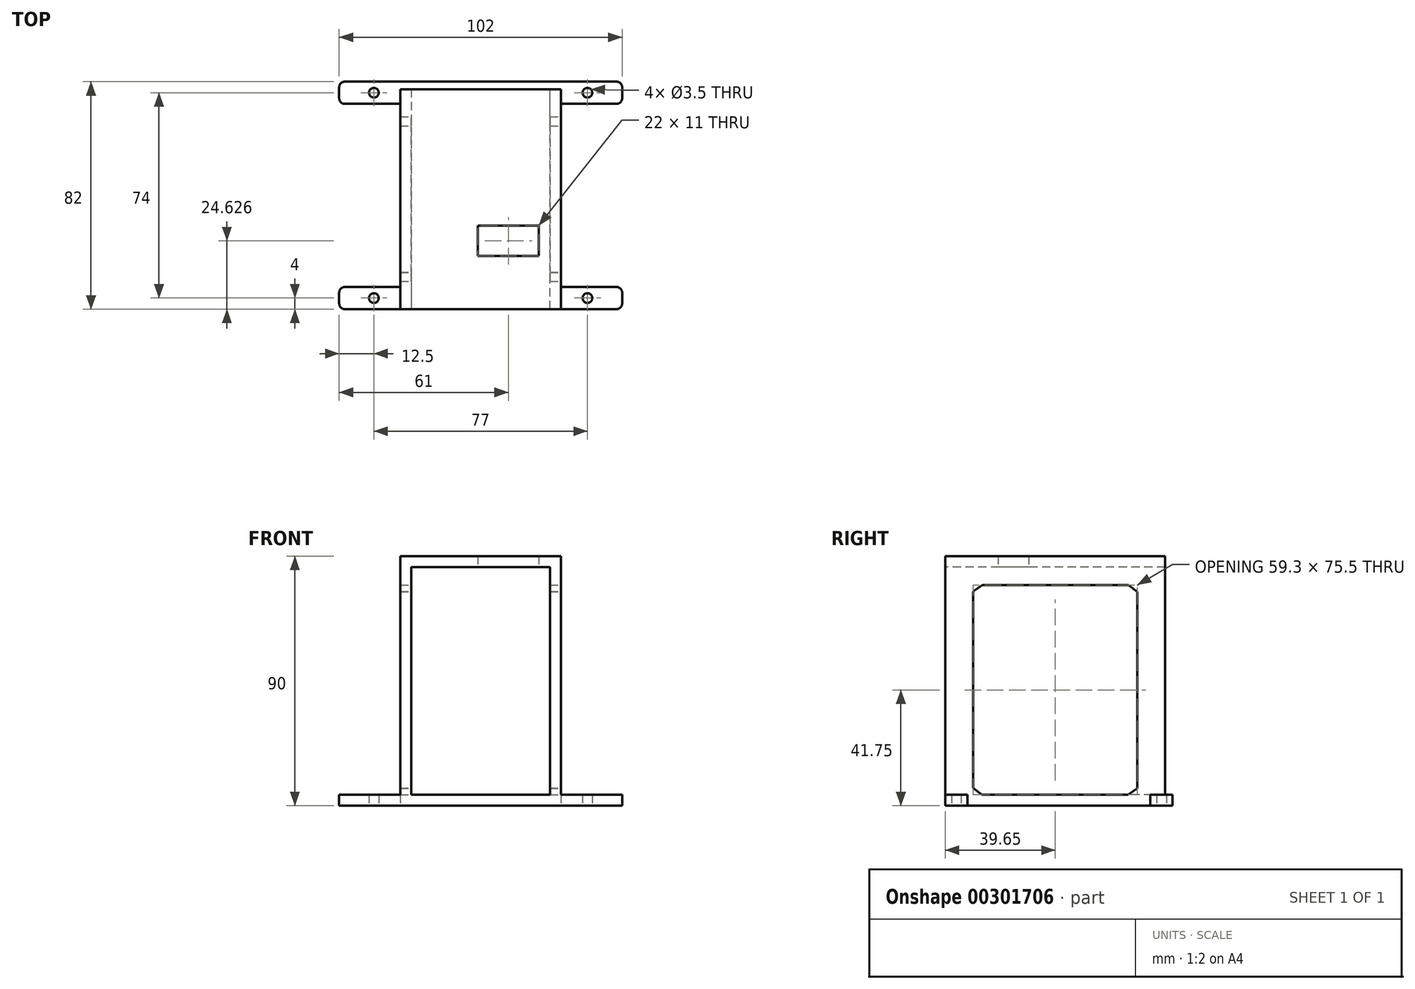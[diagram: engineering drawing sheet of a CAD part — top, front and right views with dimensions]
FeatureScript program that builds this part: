
annotation { "Feature Type Name" : "Feature", "Feature Type Description" : "" }
export const myFeature = defineFeature(function(context is Context, id is Id, definition is map)
    precondition{}
    {
        {
            var Q0;
            Q0=qCreatedBy(makeId("Top.planeOp"),FACE);
            var sketch = newSketch(context, id + "F0", { "sketchPlane" : qUnion([Q0])});
            skPoint(sketch, "E0.middle", {"position": v(45, 2.5) * mm});
            skPoint(sketch, "E1.orphan", {"position": v(-8, 87) * mm});
            skPoint(sketch, "E2.orphan", {"position": v(98, 87) * mm});
            skPoint(sketch, "E3.orphan", {"position": v(-8, 10) * mm});
            skPoint(sketch, "E4.orphan", {"position": v(0, 0) * mm});
            skPoint(sketch, "E5.orphan", {"position": v(90, 0) * mm});
            skPoint(sketch, "E6", {"position": v(45, 104.4) * mm});
            skPoint(sketch, "E7.end.orphan", {"position": v(95.45, 87) * mm});
            skPoint(sketch, "E8.bottom.end.orphan", {"position": v(33.96, 3.68) * mm});
            skLineSegment(sketch, "E9.bottom", {"start": v(19, 89.45) * mm, "end": v(71, 89.45) * mm});
            skLineSegment(sketch, "E9.top", {"start": v(19, 7.45) * mm, "end": v(71, 7.45) * mm});
            skLineSegment(sketch, "E9.left", {"start": v(19, 81.45) * mm, "end": v(19, 15.45) * mm});
            skLineSegment(sketch, "E9.right", {"start": v(71, 81.45) * mm, "end": v(71, 15.45) * mm});
            skLineSegment(sketch, "E10.bottom", {"start": v(71, 89.45) * mm, "end": v(96, 89.45) * mm});
            skLineSegment(sketch, "E10.top", {"start": v(71, 81.45) * mm, "end": v(96, 81.45) * mm});
            skLineSegment(sketch, "E10.right", {"start": v(96, 89.45) * mm, "end": v(96, 81.45) * mm});
            skLineSegment(sketch, "E11.bottom", {"start": v(19, 89.45) * mm, "end": v(-6, 89.45) * mm});
            skLineSegment(sketch, "E11.top", {"start": v(19, 81.45) * mm, "end": v(-6, 81.45) * mm});
            skLineSegment(sketch, "E11.right", {"start": v(-6, 89.45) * mm, "end": v(-6, 81.45) * mm});
            skLineSegment(sketch, "E12.bottom", {"start": v(19, 7.45) * mm, "end": v(-6, 7.45) * mm});
            skLineSegment(sketch, "E12.top", {"start": v(19, 15.45) * mm, "end": v(-6, 15.45) * mm});
            skLineSegment(sketch, "E12.right", {"start": v(-6, 7.45) * mm, "end": v(-6, 15.45) * mm});
            skLineSegment(sketch, "E13.bottom", {"start": v(71, 7.45) * mm, "end": v(96, 7.45) * mm});
            skLineSegment(sketch, "E13.top", {"start": v(71, 15.45) * mm, "end": v(96, 15.45) * mm});
            skLineSegment(sketch, "E13.right", {"start": v(96, 7.45) * mm, "end": v(96, 15.45) * mm});
            skLineSegment(sketch, "E14", {"start": v(19, 7.45) * mm, "end": v(-6, 15.45) * mm, "construction": true});
            skLineSegment(sketch, "E15", {"start": v(-6, 7.45) * mm, "end": v(19, 15.45) * mm, "construction": true});
            skCircle(sketch, "E16", {"center": v(6.5, 11.45) * mm, "radius": 1.75 * mm});
            skLineSegment(sketch, "E17", {"start": v(96, 7.45) * mm, "end": v(71, 15.45) * mm, "construction": true});
            skLineSegment(sketch, "E18", {"start": v(71, 7.45) * mm, "end": v(96, 15.45) * mm, "construction": true});
            skCircle(sketch, "E19", {"center": v(83.5, 11.45) * mm, "radius": 1.75 * mm});
            skLineSegment(sketch, "E20", {"start": v(96, 81.45) * mm, "end": v(71, 89.45) * mm, "construction": true});
            skLineSegment(sketch, "E21", {"start": v(71, 81.45) * mm, "end": v(96, 89.45) * mm, "construction": true});
            skCircle(sketch, "E22", {"center": v(83.5, 85.45) * mm, "radius": 1.75 * mm});
            skLineSegment(sketch, "E23", {"start": v(19, 81.45) * mm, "end": v(-6, 89.45) * mm, "construction": true});
            skLineSegment(sketch, "E24", {"start": v(-6, 81.45) * mm, "end": v(19, 89.45) * mm, "construction": true});
            skCircle(sketch, "E25", {"center": v(6.5, 85.45) * mm, "radius": 1.75 * mm});
            skSolve(sketch);
        }
        {
            var Q0;
            Q0=makeQuery(id+"F0.imprint","IMPRINT",FACE,{"disambiguationData":[TD([[makeQuery(id+"F0.imprint","IMPRINT",EDGE,{"derivedFrom":sQuery(id+"F0.wireOp",EDGE,"E9.bottom")}),-1.0]])]});
            extrude(context, id + "F1", {"entities" : qUnion([Q0]), "depth" : 4 * mm, "offsetDistance" : 25 * mm});
        }
        {
            var Q0;
            Q0=makeQuery(id+"F1.opExtrude","CAP_FACE",FACE,{"disambiguationData":[OSD([sQuery(id+"F0.wireOp",EDGE,"E9.bottom"),sQuery(id+"F0.wireOp",EDGE,"E9.top"),sQuery(id+"F0.wireOp",EDGE,"E9.left"),sQuery(id+"F0.wireOp",EDGE,"E9.right"),sQuery(id+"F0.wireOp",EDGE,"E10.bottom"),sQuery(id+"F0.wireOp",EDGE,"E10.top"),sQuery(id+"F0.wireOp",EDGE,"E10.right"),sQuery(id+"F0.wireOp",EDGE,"E11.bottom"),sQuery(id+"F0.wireOp",EDGE,"E11.top"),sQuery(id+"F0.wireOp",EDGE,"E11.right"),sQuery(id+"F0.wireOp",EDGE,"E12.bottom"),sQuery(id+"F0.wireOp",EDGE,"E12.top"),sQuery(id+"F0.wireOp",EDGE,"E12.right"),sQuery(id+"F0.wireOp",EDGE,"E13.bottom"),sQuery(id+"F0.wireOp",EDGE,"E13.top"),sQuery(id+"F0.wireOp",EDGE,"E13.right"),sQuery(id+"F0.wireOp",EDGE,"E16"),sQuery(id+"F0.wireOp",EDGE,"E19"),sQuery(id+"F0.wireOp",EDGE,"E22"),sQuery(id+"F0.wireOp",EDGE,"E25")])],"isStart":false});
            cPlane(context, id + "F2", {"entities" : qUnion([Q0]), "cplaneType" : CPlaneType.OFFSET, "offset" : 0 * mm, "width" : 150 * mm, "height" : 150 * mm});
        }
        {
            var Q0;
            Q0=qCreatedBy(id+"F2.planeOp",FACE);
            var sketch = newSketch(context, id + "F3", { "sketchPlane" : qUnion([Q0])});
            skLineSegment(sketch, "E26.bottom", {"start": v(68, 7.45) * mm, "end": v(71, 7.45) * mm});
            skLineSegment(sketch, "E26.top", {"start": v(68, 86.75) * mm, "end": v(71, 86.75) * mm});
            skLineSegment(sketch, "E26.left", {"start": v(68, 7.45) * mm, "end": v(68, 86.75) * mm});
            skLineSegment(sketch, "E26.right", {"start": v(71, 7.45) * mm, "end": v(71, 86.75) * mm});
            skLineSegment(sketch, "E27.bottom", {"start": v(19, 86.75) * mm, "end": v(22, 86.75) * mm});
            skLineSegment(sketch, "E27.top", {"start": v(19, 7.45) * mm, "end": v(22, 7.45) * mm});
            skLineSegment(sketch, "E27.left", {"start": v(19, 86.75) * mm, "end": v(19, 7.45) * mm});
            skLineSegment(sketch, "E27.right", {"start": v(22, 86.75) * mm, "end": v(22, 7.45) * mm});
            skSolve(sketch);
        }
        {
            var Q0;
            Q0=makeQuery(id+"F3.imprint","IMPRINT",FACE,{"disambiguationData":[TD([[makeQuery(id+"F3.imprint","IMPRINT",EDGE,{"derivedFrom":sQuery(id+"F3.wireOp",EDGE,"E27.bottom")}),-1.0]])]});
            var Q1;
            Q1=makeQuery(id+"F3.imprint","IMPRINT",FACE,{"disambiguationData":[TD([[makeQuery(id+"F3.imprint","IMPRINT",EDGE,{"derivedFrom":sQuery(id+"F3.wireOp",EDGE,"E26.bottom")}),1.0]])]});
            extrude(context, id + "F4", {"entities" : qUnion([Q0, Q1]), "operationType" : NewBodyOperationType.ADD, "depth" : 82 * mm, "offsetDistance" : 25 * mm});
        }
        {
            var Q0;
            Q0=makeQuery(id+"F4.opExtrude","SWEPT_FACE",FACE,{"disambiguationData":[OSD([sQuery(id+"F3.wireOp",EDGE,"E27.right")])]});
            extrude(context, id + "F5", {"entities" : qUnion([Q0]), "operationType" : NewBodyOperationType.REMOVE, "oppositeDirection" : true, "depth" : 2 * mm, "offsetDistance" : 25 * mm});
        }
        {
            var Q0;
            Q0=makeQuery(id+"F4.opExtrude","SWEPT_FACE",FACE,{"disambiguationData":[OSD([sQuery(id+"F3.wireOp",EDGE,"E26.left")])]});
            extrude(context, id + "F6", {"entities" : qUnion([Q0]), "operationType" : NewBodyOperationType.REMOVE, "oppositeDirection" : true, "depth" : 2 * mm, "offsetDistance" : 25 * mm});
        }
        {
            var Q0;
            Q0=makeQuery(id+"F4.boolean.opBoolean","MERGE",FACE,{"derivedFrom":[makeQuery(id+"F1.opExtrude","SWEPT_FACE",FACE,{"disambiguationData":[OSD([sQuery(id+"F0.wireOp",EDGE,"E9.right")])]}),makeQuery(id+"F4.opExtrude","SWEPT_FACE",FACE,{"disambiguationData":[OSD([sQuery(id+"F3.wireOp",EDGE,"E26.right")])]})]});
            extrude(context, id + "F7", {"entities" : qUnion([Q0]), "operationType" : NewBodyOperationType.ADD, "depth" : 3 * mm, "offsetDistance" : 25 * mm});
        }
        {
            var Q0;
            Q0=makeQuery(id+"F4.boolean.opBoolean","MERGE",FACE,{"derivedFrom":[makeQuery(id+"F1.opExtrude","SWEPT_FACE",FACE,{"disambiguationData":[OSD([sQuery(id+"F0.wireOp",EDGE,"E9.left")])]}),makeQuery(id+"F4.opExtrude","SWEPT_FACE",FACE,{"disambiguationData":[OSD([sQuery(id+"F3.wireOp",EDGE,"E27.left")])]})]});
            extrude(context, id + "F8", {"entities" : qUnion([Q0]), "operationType" : NewBodyOperationType.ADD, "depth" : 3 * mm, "offsetDistance" : 25 * mm});
        }
        {
            var Q0;
            Q0=makeQuery(id+"F1.opExtrude","SWEPT_EDGE",EDGE,{"disambiguationData":[OSD([sQuery(id+"F0.wireOp",EDGE,"E10.top"),sQuery(id+"F0.wireOp",EDGE,"E10.right")])]});
            var Q1;
            Q1=makeQuery(id+"F1.opExtrude","SWEPT_EDGE",EDGE,{"disambiguationData":[OSD([sQuery(id+"F0.wireOp",EDGE,"E10.bottom"),sQuery(id+"F0.wireOp",EDGE,"E10.right")])]});
            var Q2;
            Q2=makeQuery(id+"F1.opExtrude","SWEPT_EDGE",EDGE,{"disambiguationData":[OSD([sQuery(id+"F0.wireOp",EDGE,"E13.top"),sQuery(id+"F0.wireOp",EDGE,"E13.right")])]});
            var Q3;
            Q3=makeQuery(id+"F1.opExtrude","SWEPT_EDGE",EDGE,{"disambiguationData":[OSD([sQuery(id+"F0.wireOp",EDGE,"E13.bottom"),sQuery(id+"F0.wireOp",EDGE,"E13.right")])]});
            var Q4;
            Q4=makeQuery(id+"F1.opExtrude","SWEPT_EDGE",EDGE,{"disambiguationData":[OSD([sQuery(id+"F0.wireOp",EDGE,"E12.bottom"),sQuery(id+"F0.wireOp",EDGE,"E12.right")])]});
            var Q5;
            Q5=makeQuery(id+"F1.opExtrude","SWEPT_EDGE",EDGE,{"disambiguationData":[OSD([sQuery(id+"F0.wireOp",EDGE,"E11.bottom"),sQuery(id+"F0.wireOp",EDGE,"E11.right")])]});
            var Q6;
            Q6=makeQuery(id+"F1.opExtrude","SWEPT_EDGE",EDGE,{"disambiguationData":[OSD([sQuery(id+"F0.wireOp",EDGE,"E11.top"),sQuery(id+"F0.wireOp",EDGE,"E11.right")])]});
            var Q7;
            Q7=makeQuery(id+"F1.opExtrude","SWEPT_EDGE",EDGE,{"disambiguationData":[OSD([sQuery(id+"F0.wireOp",EDGE,"E12.top"),sQuery(id+"F0.wireOp",EDGE,"E12.right")])]});
            fillet(context, id + "F9", {"entities" : qUnion([Q0, Q1, Q2, Q3, Q4, Q5, Q6, Q7]), "radius" : 2 * mm, "tangentPropagation" : true, "allowEdgeOverflow" : false});
        }
        {
            var Q0;
            Q0=makeQuery(id+"F7.opExtrude","CAP_FACE",FACE,{"disambiguationData":[OSD([sQuery(id+"F0.wireOp",EDGE,"E9.right"),sQuery(id+"F3.wireOp",EDGE,"E26.right")])],"isStart":false});
            cPlane(context, id + "F10", {"entities" : qUnion([Q0]), "cplaneType" : CPlaneType.OFFSET, "offset" : 0 * mm, "width" : 150 * mm, "height" : 150 * mm});
        }
        {
            var Q0;
            Q0=qCreatedBy(id+"F10.planeOp",FACE);
            var sketch = newSketch(context, id + "F11", { "sketchPlane" : qUnion([Q0])});
            skLineSegment(sketch, "E28.bottom", {"start": v(17.45, 79.5) * mm, "end": v(76.75, 79.5) * mm});
            skLineSegment(sketch, "E28.top", {"start": v(17.45, 4) * mm, "end": v(76.75, 4) * mm});
            skLineSegment(sketch, "E28.left", {"start": v(17.45, 79.5) * mm, "end": v(17.45, 4) * mm});
            skLineSegment(sketch, "E28.right", {"start": v(76.75, 79.5) * mm, "end": v(76.75, 4) * mm});
            skLineSegment(sketch, "E29", {"start": v(17.45, 77.25) * mm, "end": v(20.76, 79.5) * mm});
            skLineSegment(sketch, "E30", {"start": v(76.75, 6.25) * mm, "end": v(73.44, 4) * mm});
            skLineSegment(sketch, "E31", {"start": v(73.49, 79.5) * mm, "end": v(76.75, 77.18) * mm});
            skLineSegment(sketch, "E32", {"start": v(20.67, 4) * mm, "end": v(17.45, 6.38) * mm});
            skSolve(sketch);
        }
        {
            var Q0;
            {var subQ3=sQuery(id+"F11.wireOp",EDGE,"E29");Q0=makeQuery(id+"F11.imprint","IMPRINT",FACE,{"disambiguationData":[TD([[makeQuery(id+"F11.imprint","IMPRINT",EDGE,{"derivedFrom":subQ3}),-1.0]])]});}
            extrude(context, id + "F12", {"entities" : qUnion([Q0]), "operationType" : NewBodyOperationType.REMOVE, "endBound" : BoundingType.THROUGH_ALL, "oppositeDirection" : true, "depth" : 25 * mm, "offsetDistance" : 25 * mm});
        }
        {
            var Q0;
            {var subQ0=sQuery(id+"F3.wireOp",EDGE,"E27.left");Q0=makeQuery(id+"F8.boolean.opBoolean","MERGE",FACE,{"derivedFrom":[makeQuery(id+"F4.opExtrude","CAP_FACE",FACE,{"disambiguationData":[OSD([sQuery(id+"F3.wireOp",EDGE,"E27.bottom"),sQuery(id+"F3.wireOp",EDGE,"E27.top"),subQ0,sQuery(id+"F3.wireOp",EDGE,"E27.right")])],"isStart":false}),makeQuery(id+"F8.opExtrude","SWEPT_FACE",FACE,{"disambiguationData":[OSD([subQ0]),TDD([makeQuery(id+"F4.opExtrude","CAP_EDGE",EDGE,{"disambiguationData":[OSD([subQ0])],"isStart":false})])]})]});}
            cPlane(context, id + "F13", {"entities" : qUnion([Q0]), "cplaneType" : CPlaneType.OFFSET, "offset" : 0 * mm, "width" : 150 * mm, "height" : 150 * mm});
        }
        {
            var Q0;
            Q0=qCreatedBy(id+"F13.planeOp",FACE);
            var sketch = newSketch(context, id + "F14", { "sketchPlane" : qUnion([Q0])});
            skLineSegment(sketch, "E33.bottom", {"start": v(16, 86.75) * mm, "end": v(74, 86.75) * mm});
            skLineSegment(sketch, "E33.top", {"start": v(16, 7.45) * mm, "end": v(74, 7.45) * mm});
            skLineSegment(sketch, "E33.left", {"start": v(16, 86.75) * mm, "end": v(16, 7.45) * mm});
            skLineSegment(sketch, "E33.right", {"start": v(74, 86.75) * mm, "end": v(74, 7.45) * mm});
            skLineSegment(sketch, "E34.bottom", {"start": v(44, 37.58) * mm, "end": v(66, 37.58) * mm});
            skLineSegment(sketch, "E34.top", {"start": v(44, 26.58) * mm, "end": v(66, 26.58) * mm});
            skLineSegment(sketch, "E34.left", {"start": v(44, 37.58) * mm, "end": v(44, 26.58) * mm});
            skLineSegment(sketch, "E34.right", {"start": v(66, 37.58) * mm, "end": v(66, 26.58) * mm});
            skSolve(sketch);
        }
        {
            var Q0;
            Q0=makeQuery(id+"F14.imprint","IMPRINT",FACE,{"disambiguationData":[TD([[makeQuery(id+"F14.imprint","IMPRINT",EDGE,{"derivedFrom":sQuery(id+"F14.wireOp",EDGE,"E33.bottom")}),-1.0]])]});
            extrude(context, id + "F15", {"entities" : qUnion([Q0]), "operationType" : NewBodyOperationType.ADD, "depth" : 4 * mm, "offsetDistance" : 25 * mm});
        }
    });
